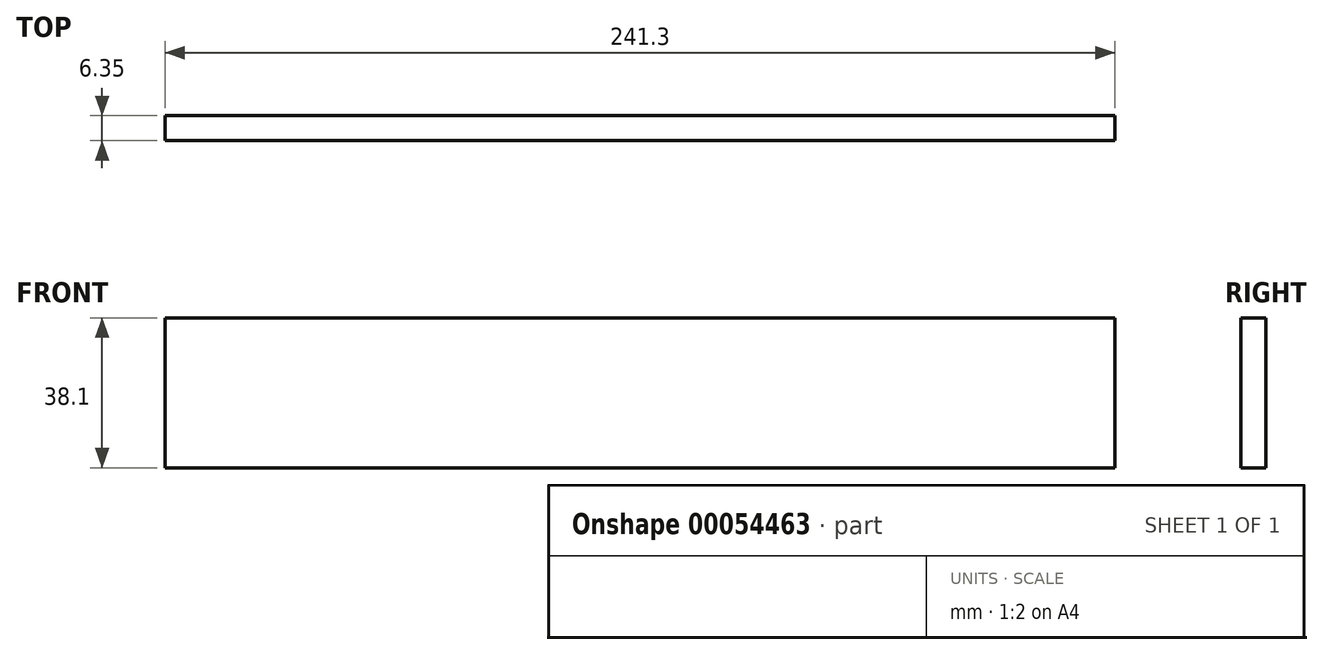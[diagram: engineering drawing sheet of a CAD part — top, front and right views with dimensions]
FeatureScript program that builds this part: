
annotation { "Feature Type Name" : "Feature", "Feature Type Description" : "" }
export const myFeature = defineFeature(function(context is Context, id is Id, definition is map)
    precondition{}
    {
        {
            var Q0;
            Q0=qCreatedBy(makeId("Front.planeOp"),FACE);
            var sketch = newSketch(context, id + "F0", { "sketchPlane" : qUnion([Q0])});
            skLineSegment(sketch, "E0.rect.bottom", {"start": v(120.65, 19.05) * mm, "end": v(-120.65, 19.05) * mm});
            skLineSegment(sketch, "E0.rect.top", {"start": v(120.65, -19.05) * mm, "end": v(-120.65, -19.05) * mm});
            skLineSegment(sketch, "E0.rect.left", {"start": v(120.65, 19.05) * mm, "end": v(120.65, -19.05) * mm});
            skLineSegment(sketch, "E0.rect.right", {"start": v(-120.65, 19.05) * mm, "end": v(-120.65, -19.05) * mm});
            skPoint(sketch, "E0.rect.middle", {"position": v(0, 0) * mm});
            skSolve(sketch);
        }
        {
            var Q0;
            Q0 = qSketchRegion(id + "F0", true);
            extrude(context, id + "F1", {"entities" : qUnion([Q0]), "oppositeDirection" : true, "depth" : 6.35 * mm});
        }
    });
